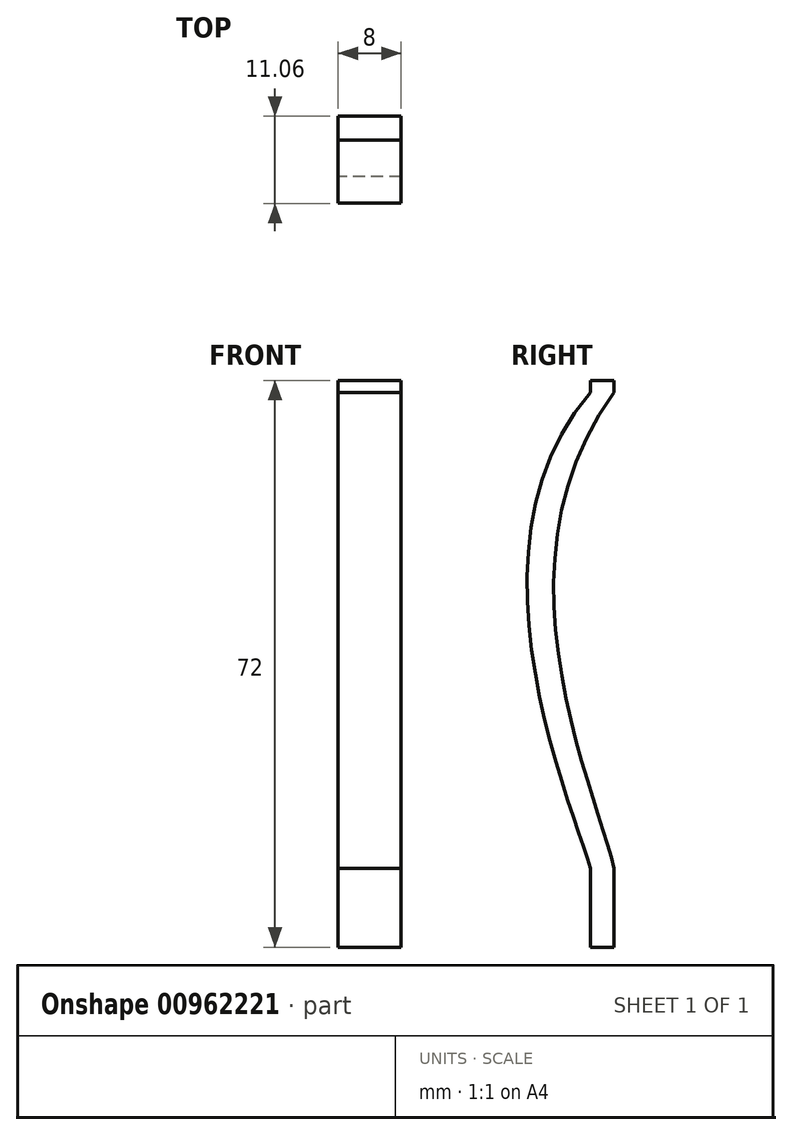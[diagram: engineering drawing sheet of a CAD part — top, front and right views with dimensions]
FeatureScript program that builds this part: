
annotation { "Feature Type Name" : "Feature", "Feature Type Description" : "" }
export const myFeature = defineFeature(function(context is Context, id is Id, definition is map)
    precondition{}
    {
        {
            var Q0;
            Q0=qCreatedBy(makeId("Top.planeOp"),FACE);
            var sketch = newSketch(context, id + "F0", { "sketchPlane" : qUnion([Q0])});
            skLineSegment(sketch, "E0.bottom", {"start": v(-4, 15) * mm, "end": v(4, 15) * mm});
            skLineSegment(sketch, "E0.top", {"start": v(-4, -15) * mm, "end": v(4, -15) * mm});
            skLineSegment(sketch, "E0.left", {"start": v(-4, 15) * mm, "end": v(-4, -15) * mm});
            skLineSegment(sketch, "E0.right", {"start": v(4, 15) * mm, "end": v(4, -15) * mm});
            skPoint(sketch, "E0.middle", {"position": v(0, 0) * mm});
            skSolve(sketch);
        }
        {
            var Q0;
            Q0=makeQuery(id+"F0.imprint","IMPRINT",FACE,{"disambiguationData":[TD([[makeQuery(id+"F0.imprint","IMPRINT",EDGE,{"derivedFrom":sQuery(id+"F0.wireOp",EDGE,"E0.bottom")}),-1.0]])]});
            extrude(context, id + "F1", {"entities" : qUnion([Q0]), "depth" : 57 * mm, "offsetDistance" : 25 * mm});
        }
        {
            var Q0;
            Q0=makeQuery(id+"F1.opExtrude","CAP_FACE",FACE,{"disambiguationData":[OSD([sQuery(id+"F0.wireOp",EDGE,"E0.bottom"),sQuery(id+"F0.wireOp",EDGE,"E0.top"),sQuery(id+"F0.wireOp",EDGE,"E0.left"),sQuery(id+"F0.wireOp",EDGE,"E0.right")])],"isStart":true});
            extrude(context, id + "F2", {"entities" : qUnion([Q0]), "operationType" : NewBodyOperationType.ADD, "depth" : 15 * mm, "offsetDistance" : 25 * mm});
        }
        {
            var Q0;
            Q0=makeQuery(id+"F1.opExtrude","SWEPT_FACE",FACE,{"disambiguationData":[OSD([sQuery(id+"F0.wireOp",EDGE,"E0.left")])]});
            var sketch = newSketch(context, id + "F3", { "sketchPlane" : qUnion([Q0])});
            skLineSegment(sketch, "E1", {"start": v(-15, 57) * mm, "end": v(-15, 55.47) * mm});
            skLineSegment(sketch, "E2", {"start": v(-15, -20.01) * mm, "end": v(-15, -5) * mm});
            skFitSpline(sketch, "E3", {"points": [v(-15, 55.47) * mm, v(-15, -5) * mm], "startDerivative": vector(48.16, -65.39) * mm, "endDerivative": vector(-6.96, -30.61) * mm});
            skLineSegment(sketch, "E4", {"start": v(-15, 57) * mm, "end": v(-12, 57) * mm});
            skLineSegment(sketch, "E5", {"start": v(-15, -20.01) * mm, "end": v(-12, -20.01) * mm});
            skLineSegment(sketch, "E6", {"start": v(-12, -20.01) * mm, "end": v(-12, -5) * mm});
            skLineSegment(sketch, "E7", {"start": v(-12, 57) * mm, "end": v(-12, 55.47) * mm});
            skFitSpline(sketch, "E8", {"points": [v(-12, 55.47) * mm, v(-12, -5) * mm], "startDerivative": vector(50.18, -58.27) * mm, "endDerivative": vector(-7.92, -26.58) * mm});
            skLineSegment(sketch, "E9.0", {"start": v(-15, -15) * mm, "end": v(15, -15) * mm});
            skSolve(sketch);
        }
        {
            var Q0;
            {var subQ3=sQuery(id+"F3.wireOp",EDGE,"E6");Q0=makeQuery(id+"F3.imprint","IMPRINT",FACE,{"disambiguationData":[TD([[makeQuery(id+"F3.imprint","IMPRINT",EDGE,{"derivedFrom":subQ3}),-1.0]])]});}
            var Q1;
            {var subQ0=sQuery(id+"F3.wireOp",EDGE,"E3");Q1=makeQuery(id+"F3.imprint","IMPRINT",FACE,{"disambiguationData":[TD([[makeQuery(id+"F3.imprint","IMPRINT",EDGE,{"derivedFrom":subQ0}),-1.0]])]});}
            var Q2;
            {var subQ4=sQuery(id+"F3.wireOp",EDGE,"E7");Q2=makeQuery(id+"F3.imprint","IMPRINT",FACE,{"disambiguationData":[TD([[makeQuery(id+"F3.imprint","IMPRINT",EDGE,{"derivedFrom":subQ4}),1.0]])]});}
            extrude(context, id + "F4", {"entities" : qUnion([Q0, Q1, Q2]), "operationType" : NewBodyOperationType.REMOVE, "endBound" : BoundingType.UP_TO_NEXT, "oppositeDirection" : true, "depth" : 25 * mm, "offsetDistance" : 25 * mm});
        }
    });
